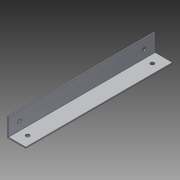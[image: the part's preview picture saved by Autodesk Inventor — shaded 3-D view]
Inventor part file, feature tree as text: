
AUTODESK INVENTOR PART (.ipt)
format: ipt  version: 2014 SP1 (Build 180222100, 222)  size: 96,768 bytes
history: native  units: in
note: dims shown in document units (in); Inventor stores cm internally (conversion verified against a paired STEP export)
features: extrude x3, sketch x3
ambient origin geometry x8: Origin, YZ Plane, XZ Plane, XY Plane, X Axis, Y Axis, Z Axis, Center Point
bodies: Solid1 (feature_tree)
feature tree (6):
  extrude  "Extrusion1"  Depth=0.0312in
  extrude  "Extrusion2"  Depth=5.0in
  extrude  "Extrusion3"  Depth=0.375in
  sketch  "Sketch1"  dims[d0=0.625in d1=0.0312in]
  sketch  "Sketch2"  dims[d2=5.0in d3=0.0in d4=0.125in]
  sketch  "Sketch3"  dims[d5=0.125in d6=0.375in d7=0.375in d8=1.0in d9=0.0in d10=0.125in d11=0.125in d12=0.375in d13=0.375in d14=1.0in d15=0.0in]
